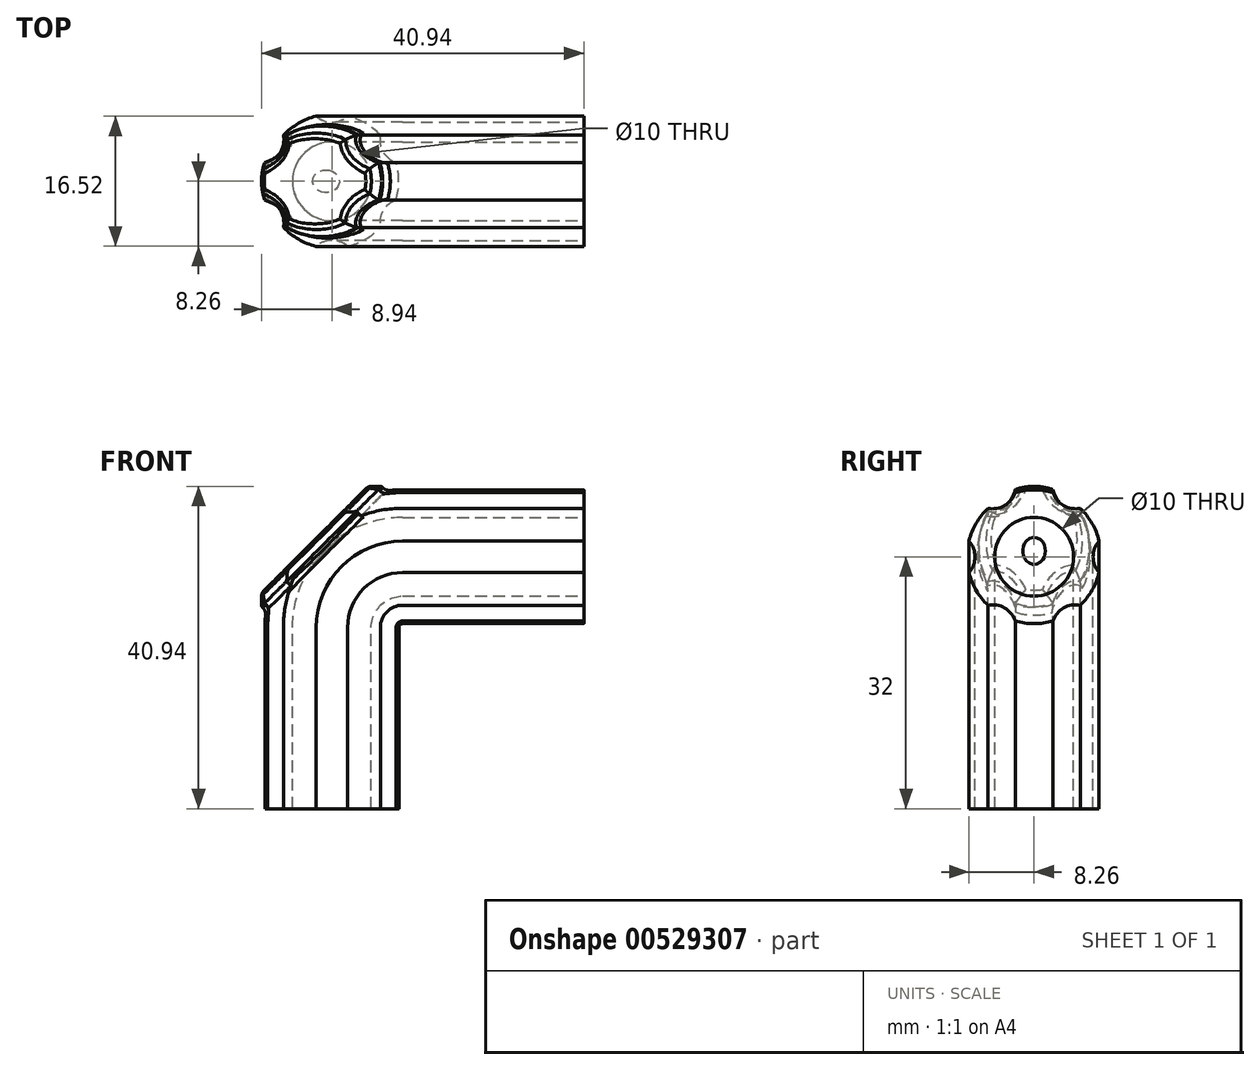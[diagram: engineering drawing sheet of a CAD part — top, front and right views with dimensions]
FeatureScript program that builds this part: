
annotation { "Feature Type Name" : "Feature", "Feature Type Description" : "" }
export const myFeature = defineFeature(function(context is Context, id is Id, definition is map)
    precondition{}
    {
        {
            var Q0;
            Q0=qCreatedBy(makeId("Top.planeOp"),FACE);
            var sketch = newSketch(context, id + "F0", { "sketchPlane" : qUnion([Q0])});
            skCircle(sketch, "E0", {"center": v(0, 0) * mm, "radius": 5 * mm});
            skCircle(sketch, "E1", {"center": v(0, 0) * mm, "radius": 8.5 * mm});
            skArc(sketch, "E2", {"start": v(-2, 8.26) * mm, "mid": v(0, 7.5) * mm, "end": v(2, 8.26) * mm});
            skArc(sketch, "E3.1.0", {"start": v(-8.15, 2.4) * mm, "mid": v(-6.5, 3.75) * mm, "end": v(-6.15, 5.86) * mm});
            skArc(sketch, "E3.2.0", {"start": v(-6.15, -5.86) * mm, "mid": v(-6.5, -3.75) * mm, "end": v(-8.15, -2.4) * mm});
            skArc(sketch, "E3.3.0", {"start": v(2, -8.26) * mm, "mid": v(0, -7.5) * mm, "end": v(-2, -8.26) * mm});
            skArc(sketch, "E3.4.0", {"start": v(8.15, -2.4) * mm, "mid": v(6.5, -3.75) * mm, "end": v(6.15, -5.86) * mm});
            skArc(sketch, "E3.5.0", {"start": v(6.15, 5.86) * mm, "mid": v(6.5, 3.75) * mm, "end": v(8.15, 2.4) * mm});
            skSolve(sketch);
        }
        {
            var Q0;
            Q0=qCreatedBy(makeId("Front.planeOp"),FACE);
            var sketch = newSketch(context, id + "F1", { "sketchPlane" : qUnion([Q0])});
            skLineSegment(sketch, "E4", {"start": v(0, 0) * mm, "end": v(0, 23) * mm});
            skLineSegment(sketch, "E5", {"start": v(9, 32) * mm, "end": v(32, 32) * mm});
            skPoint(sketch, "E6.visualSharp", {"position": v(0, 32) * mm});
            skArc(sketch, "E6.filletArc", {"start": v(9, 32) * mm, "mid": v(2.64, 29.36) * mm, "end": v(0, 23) * mm});
            skSolve(sketch);
        }
        {
            var Q0;
            Q0=makeQuery(id+"F0.imprint","IMPRINT",FACE,{"disambiguationData":[TD([[makeQuery(id+"F0.imprint","IMPRINT",EDGE,{"derivedFrom":sQuery(id+"F0.wireOp",EDGE,"E0")}),-1.0]])]});
            var Q1;
            Q1=sQuery(id+"F1.wireOp",EDGE,"E4");
            var Q2;
            Q2=sQuery(id+"F1.wireOp",EDGE,"E6.filletArc");
            var Q3;
            Q3=sQuery(id+"F1.wireOp",EDGE,"E5");
            sweep(context, id + "F2", {"profiles" : qUnion([Q0]), "path" : qUnion([Q1, Q2, Q3])});
        }
        {
            var Q0;
            Q0=qCreatedBy(makeId("Front.planeOp"),FACE);
            var sketch = newSketch(context, id + "F3", { "sketchPlane" : qUnion([Q0])});
            skLineSegment(sketch, "E7", {"start": v(0, 0) * mm, "end": v(0, 0) * mm});
            skLineSegment(sketch, "E8", {"start": v(0, 0) * mm, "end": v(0, 33.5) * mm, "construction": true});
            skLineSegment(sketch, "E9", {"start": v(0, 33.5) * mm, "end": v(14.14, 47.64) * mm, "construction": true});
            skLineSegment(sketch, "E10", {"start": v(14.14, 47.64) * mm, "end": v(-14.14, 19.36) * mm});
            skLineSegment(sketch, "E11", {"start": v(14.14, 47.64) * mm, "end": v(7.07, 54.71) * mm});
            skLineSegment(sketch, "E12", {"start": v(7.07, 54.71) * mm, "end": v(-21.21, 26.43) * mm});
            skLineSegment(sketch, "E13", {"start": v(-21.21, 26.43) * mm, "end": v(-14.14, 19.36) * mm});
            skSolve(sketch);
        }
        {
            var Q0;
            Q0=makeQuery(id+"F3.imprint","IMPRINT",FACE,{"disambiguationData":[TD([[makeQuery(id+"F3.imprint","IMPRINT",EDGE,{"derivedFrom":sQuery(id+"F3.wireOp",EDGE,"E10")}),-1.0]])]});
            extrude(context, id + "F4", {"entities" : qUnion([Q0]), "operationType" : NewBodyOperationType.REMOVE, "depth" : 25 * mm, "offsetDistance" : 25 * mm, "hasSecondDirection" : true, "secondDirectionOppositeDirection" : true, "secondDirectionDepth" : 25 * mm});
        }
        {
            var Q0;
            Q0=makeQuery(id+"F4.boolean.opBoolean","COPY",FACE,{"derivedFrom":makeQuery(id+"F4.opExtrude","SWEPT_FACE",FACE,{"disambiguationData":[OSD([sQuery(id+"F3.wireOp",EDGE,"E10")])]})});
            var sketch = newSketch(context, id + "F5", { "sketchPlane" : qUnion([Q0])});
            skLineSegment(sketch, "E14.bottom", {"start": v(-3.86, 18.92) * mm, "end": v(3.14, 18.92) * mm});
            skLineSegment(sketch, "E14.top", {"start": v(-3.86, 25.92) * mm, "end": v(3.14, 25.92) * mm});
            skLineSegment(sketch, "E14.left", {"start": v(-3.86, 18.92) * mm, "end": v(-3.86, 25.92) * mm});
            skLineSegment(sketch, "E14.right", {"start": v(3.14, 18.92) * mm, "end": v(3.14, 25.92) * mm});
            skLineSegment(sketch, "E15", {"start": v(-5.86, 28.92) * mm, "end": v(-3.86, 28.92) * mm, "construction": true});
            skLineSegment(sketch, "E16", {"start": v(-3.86, 28.92) * mm, "end": v(-3.86, 25.92) * mm, "construction": true});
            skSolve(sketch);
        }
        {
            var Q0;
            Q0=makeQuery(id+"F5.imprint","IMPRINT",FACE,{"disambiguationData":[TD([[makeQuery(id+"F5.imprint","IMPRINT",EDGE,{"derivedFrom":makeQuery(id+"F4.boolean.opBoolean","INTERSECT",EDGE,{"derivedFrom":[makeQuery(id+"F2.opSweep","SWEPT_FACE",FACE,{"disambiguationData":[OSD([sQuery(id+"F0.wireOp",EDGE,"E0"),sQuery(id+"F1.wireOp",EDGE,"E6.filletArc")])]}),makeQuery(id+"F4.opExtrude","SWEPT_FACE",FACE,{"disambiguationData":[OSD([sQuery(id+"F3.wireOp",EDGE,"E10")])]})]})}),-1.0]])]});
            var Q1;
            Q1=makeQuery(id+"F5.imprint","IMPRINT",FACE,{"disambiguationData":[TD([[makeQuery(id+"F5.imprint","IMPRINT",EDGE,{"derivedFrom":sQuery(id+"F5.wireOp",EDGE,"E14.bottom")}),1.0]])]});
            var Q2;
            Q2=makeQuery(id+"F5.imprint","IMPRINT",FACE,{"disambiguationData":[TD([[makeQuery(id+"F5.imprint","IMPRINT",EDGE,{"derivedFrom":sQuery(id+"F5.wireOp",EDGE,"E14.bottom")}),-1.0]])]});
            extrude(context, id + "F6", {"entities" : qUnion([Q0, Q1, Q2]), "operationType" : NewBodyOperationType.ADD, "depth" : 2 * mm, "offsetDistance" : 25 * mm});
        }
        {
            var Q0;
            {var subQ0=sQuery(id+"F3.wireOp",EDGE,"E10");var subQ1=sQuery(id+"F1.wireOp",EDGE,"E6.filletArc");var subQ2=sQuery(id+"F0.wireOp",EDGE,"E1");var subQ3=makeQuery(id+"F4.boolean.opBoolean","INTERSECT",EDGE,{"disambiguationData":[OD(1.0)],"derivedFrom":[makeQuery(id+"F2.opSweep","SWEPT_FACE",FACE,{"disambiguationData":[OSD([subQ2,subQ1]),TDD([makeQuery(id+"F0.imprint","IMPRINT",EDGE,{"disambiguationData":[TD([[makeQuery(id+"F0.imprint","INTERSECT",VERTEX,{"disambiguationData":[OD(0.0)],"derivedFrom":[subQ2,sQuery(id+"F0.wireOp",EDGE,"E3.1.0")]}),-1.0]])],"derivedFrom":subQ2}),subQ1])]}),makeQuery(id+"F4.opExtrude","SWEPT_FACE",FACE,{"disambiguationData":[OSD([subQ0])]})]});Q0=makeQuery(id+"F6.boolean.opBoolean","MERGE",EDGE,{"derivedFrom":[subQ3,makeQuery(id+"F6.opExtrude","CAP_EDGE",EDGE,{"disambiguationData":[OSD([subQ2,subQ1,subQ0]),TDD([makeQuery(id+"F5.imprint","IMPRINT",EDGE,{"derivedFrom":subQ3})])],"isStart":true})]});}
            var Q1;
            {var subQ0=sQuery(id+"F3.wireOp",EDGE,"E10");var subQ1=sQuery(id+"F1.wireOp",EDGE,"E6.filletArc");var subQ2=sQuery(id+"F0.wireOp",EDGE,"E3.1.0");var subQ3=makeQuery(id+"F4.boolean.opBoolean","INTERSECT",EDGE,{"disambiguationData":[OD(1.0)],"derivedFrom":[makeQuery(id+"F2.opSweep","SWEPT_FACE",FACE,{"disambiguationData":[OSD([subQ2,subQ1])]}),makeQuery(id+"F4.opExtrude","SWEPT_FACE",FACE,{"disambiguationData":[OSD([subQ0])]})]});Q1=makeQuery(id+"F6.boolean.opBoolean","MERGE",EDGE,{"derivedFrom":[subQ3,makeQuery(id+"F6.opExtrude","CAP_EDGE",EDGE,{"disambiguationData":[OSD([subQ2,subQ1,subQ0]),TDD([makeQuery(id+"F5.imprint","IMPRINT",EDGE,{"derivedFrom":subQ3})])],"isStart":true})]});}
            var Q2;
            {var subQ0=sQuery(id+"F3.wireOp",EDGE,"E10");var subQ1=sQuery(id+"F1.wireOp",EDGE,"E6.filletArc");var subQ2=sQuery(id+"F0.wireOp",EDGE,"E1");var subQ3=makeQuery(id+"F4.boolean.opBoolean","INTERSECT",EDGE,{"derivedFrom":[makeQuery(id+"F2.opSweep","SWEPT_FACE",FACE,{"disambiguationData":[OSD([subQ2,subQ1]),TDD([makeQuery(id+"F0.imprint","IMPRINT",EDGE,{"disambiguationData":[TD([[makeQuery(id+"F0.imprint","INTERSECT",VERTEX,{"disambiguationData":[OD(0.0)],"derivedFrom":[subQ2,sQuery(id+"F0.wireOp",EDGE,"E2")]}),-1.0]])],"derivedFrom":subQ2}),subQ1])]}),makeQuery(id+"F4.opExtrude","SWEPT_FACE",FACE,{"disambiguationData":[OSD([subQ0])]})]});Q2=makeQuery(id+"F6.boolean.opBoolean","MERGE",EDGE,{"derivedFrom":[subQ3,makeQuery(id+"F6.opExtrude","CAP_EDGE",EDGE,{"disambiguationData":[OSD([subQ2,subQ1,subQ0]),TDD([makeQuery(id+"F5.imprint","IMPRINT",EDGE,{"derivedFrom":subQ3})])],"isStart":true})]});}
            var Q3;
            {var subQ0=sQuery(id+"F3.wireOp",EDGE,"E10");var subQ1=sQuery(id+"F1.wireOp",EDGE,"E6.filletArc");var subQ2=sQuery(id+"F0.wireOp",EDGE,"E3.1.0");var subQ3=makeQuery(id+"F4.boolean.opBoolean","INTERSECT",EDGE,{"disambiguationData":[OD(0.0)],"derivedFrom":[makeQuery(id+"F2.opSweep","SWEPT_FACE",FACE,{"disambiguationData":[OSD([subQ2,subQ1])]}),makeQuery(id+"F4.opExtrude","SWEPT_FACE",FACE,{"disambiguationData":[OSD([subQ0])]})]});Q3=makeQuery(id+"F6.boolean.opBoolean","MERGE",EDGE,{"derivedFrom":[subQ3,makeQuery(id+"F6.opExtrude","CAP_EDGE",EDGE,{"disambiguationData":[OSD([subQ2,subQ1,subQ0]),TDD([makeQuery(id+"F5.imprint","IMPRINT",EDGE,{"derivedFrom":subQ3})])],"isStart":true})]});}
            var Q4;
            {var subQ0=sQuery(id+"F3.wireOp",EDGE,"E10");var subQ1=sQuery(id+"F1.wireOp",EDGE,"E6.filletArc");var subQ2=sQuery(id+"F0.wireOp",EDGE,"E1");var subQ3=makeQuery(id+"F4.boolean.opBoolean","INTERSECT",EDGE,{"disambiguationData":[OD(0.0)],"derivedFrom":[makeQuery(id+"F2.opSweep","SWEPT_FACE",FACE,{"disambiguationData":[OSD([subQ2,subQ1]),TDD([makeQuery(id+"F0.imprint","IMPRINT",EDGE,{"disambiguationData":[TD([[makeQuery(id+"F0.imprint","INTERSECT",VERTEX,{"disambiguationData":[OD(0.0)],"derivedFrom":[subQ2,sQuery(id+"F0.wireOp",EDGE,"E3.1.0")]}),-1.0]])],"derivedFrom":subQ2}),subQ1])]}),makeQuery(id+"F4.opExtrude","SWEPT_FACE",FACE,{"disambiguationData":[OSD([subQ0])]})]});Q4=makeQuery(id+"F6.boolean.opBoolean","MERGE",EDGE,{"derivedFrom":[subQ3,makeQuery(id+"F6.opExtrude","CAP_EDGE",EDGE,{"disambiguationData":[OSD([subQ2,subQ1,subQ0]),TDD([makeQuery(id+"F5.imprint","IMPRINT",EDGE,{"derivedFrom":subQ3})])],"isStart":true})]});}
            var Q5;
            {var subQ0=sQuery(id+"F3.wireOp",EDGE,"E10");var subQ1=sQuery(id+"F1.wireOp",EDGE,"E6.filletArc");var subQ2=sQuery(id+"F0.wireOp",EDGE,"E3.2.0");var subQ3=makeQuery(id+"F4.boolean.opBoolean","INTERSECT",EDGE,{"disambiguationData":[OD(0.0)],"derivedFrom":[makeQuery(id+"F2.opSweep","SWEPT_FACE",FACE,{"disambiguationData":[OSD([subQ2,subQ1])]}),makeQuery(id+"F4.opExtrude","SWEPT_FACE",FACE,{"disambiguationData":[OSD([subQ0])]})]});Q5=makeQuery(id+"F6.boolean.opBoolean","MERGE",EDGE,{"derivedFrom":[subQ3,makeQuery(id+"F6.opExtrude","CAP_EDGE",EDGE,{"disambiguationData":[OSD([subQ2,subQ1,subQ0]),TDD([makeQuery(id+"F5.imprint","IMPRINT",EDGE,{"derivedFrom":subQ3})])],"isStart":true})]});}
            var Q6;
            {var subQ0=sQuery(id+"F3.wireOp",EDGE,"E10");var subQ1=sQuery(id+"F1.wireOp",EDGE,"E6.filletArc");var subQ2=sQuery(id+"F0.wireOp",EDGE,"E1");var subQ3=makeQuery(id+"F4.boolean.opBoolean","INTERSECT",EDGE,{"derivedFrom":[makeQuery(id+"F2.opSweep","SWEPT_FACE",FACE,{"disambiguationData":[OSD([subQ2,subQ1]),TDD([makeQuery(id+"F0.imprint","IMPRINT",EDGE,{"disambiguationData":[TD([[makeQuery(id+"F0.imprint","INTERSECT",VERTEX,{"disambiguationData":[OD(0.0)],"derivedFrom":[subQ2,sQuery(id+"F0.wireOp",EDGE,"E3.2.0")]}),-1.0]])],"derivedFrom":subQ2}),subQ1])]}),makeQuery(id+"F4.opExtrude","SWEPT_FACE",FACE,{"disambiguationData":[OSD([subQ0])]})]});Q6=makeQuery(id+"F6.boolean.opBoolean","MERGE",EDGE,{"derivedFrom":[subQ3,makeQuery(id+"F6.opExtrude","CAP_EDGE",EDGE,{"disambiguationData":[OSD([subQ2,subQ1,subQ0]),TDD([makeQuery(id+"F5.imprint","IMPRINT",EDGE,{"derivedFrom":subQ3})])],"isStart":true})]});}
            var Q7;
            {var subQ0=sQuery(id+"F3.wireOp",EDGE,"E10");var subQ1=sQuery(id+"F1.wireOp",EDGE,"E6.filletArc");var subQ2=sQuery(id+"F0.wireOp",EDGE,"E3.2.0");var subQ3=makeQuery(id+"F4.boolean.opBoolean","INTERSECT",EDGE,{"disambiguationData":[OD(1.0)],"derivedFrom":[makeQuery(id+"F2.opSweep","SWEPT_FACE",FACE,{"disambiguationData":[OSD([subQ2,subQ1])]}),makeQuery(id+"F4.opExtrude","SWEPT_FACE",FACE,{"disambiguationData":[OSD([subQ0])]})]});Q7=makeQuery(id+"F6.boolean.opBoolean","MERGE",EDGE,{"derivedFrom":[subQ3,makeQuery(id+"F6.opExtrude","CAP_EDGE",EDGE,{"disambiguationData":[OSD([subQ2,subQ1,subQ0]),TDD([makeQuery(id+"F5.imprint","IMPRINT",EDGE,{"derivedFrom":subQ3})])],"isStart":true})]});}
            fillet(context, id + "F7", {"entities" : qUnion([Q0, Q1, Q2, Q3, Q4, Q5, Q6, Q7]), "radius" : 1.2 * mm, "tangentPropagation" : true, "allowEdgeOverflow" : false});
        }
        {
            var Q0;
            Q0=makeQuery(id+"F6.opExtrude","CAP_FACE",FACE,{"disambiguationData":[OSD([sQuery(id+"F0.wireOp",EDGE,"E1"),sQuery(id+"F0.wireOp",EDGE,"E3.1.0"),sQuery(id+"F0.wireOp",EDGE,"E3.2.0"),sQuery(id+"F1.wireOp",EDGE,"E6.filletArc"),sQuery(id+"F3.wireOp",EDGE,"E10")])],"isStart":false});
            chamfer(context, id + "F8", {"entities" : qUnion([Q0]), "width" : 1.2 * mm, "tangentPropagation" : true});
        }
        {
            var Q0;
            Q0=makeQuery(id+"F6.opExtrude","CAP_FACE",FACE,{"disambiguationData":[OSD([sQuery(id+"F0.wireOp",EDGE,"E1"),sQuery(id+"F0.wireOp",EDGE,"E3.1.0"),sQuery(id+"F0.wireOp",EDGE,"E3.2.0"),sQuery(id+"F1.wireOp",EDGE,"E6.filletArc"),sQuery(id+"F3.wireOp",EDGE,"E10")])],"isStart":false});
            fillet(context, id + "F9", {"entities" : qUnion([Q0]), "radius" : 1 * mm, "tangentPropagation" : true, "allowEdgeOverflow" : false});
        }
    });
